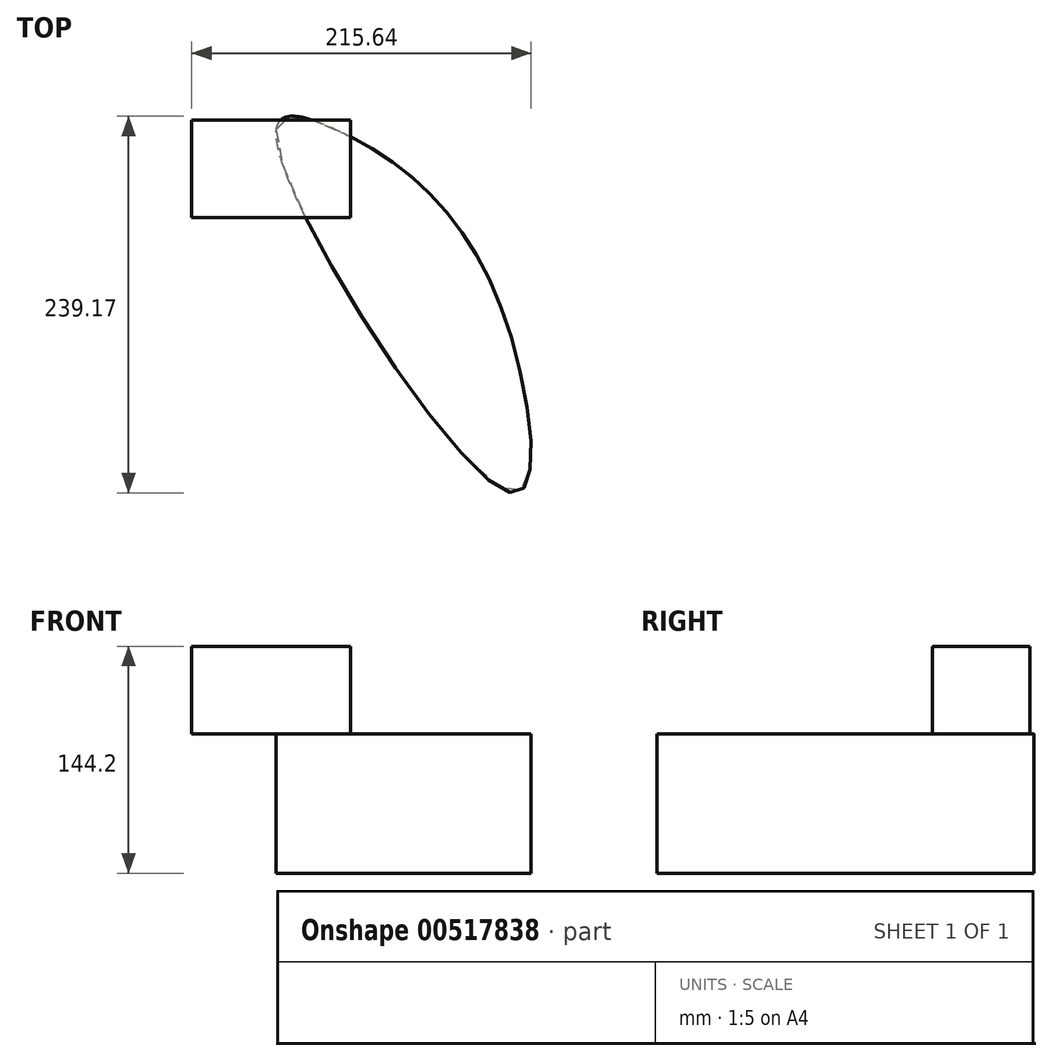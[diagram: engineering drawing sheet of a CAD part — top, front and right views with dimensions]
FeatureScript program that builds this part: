
annotation { "Feature Type Name" : "Feature", "Feature Type Description" : "" }
export const myFeature = defineFeature(function(context is Context, id is Id, definition is map)
    precondition{}
    {
        {
            var Q0;
            Q0=qCreatedBy(makeId("Top.planeOp"),FACE);
            var sketch = newSketch(context, id + "F0", { "sketchPlane" : qUnion([Q0])});
            skFitSpline(sketch, "E0", {"points": [v(-65.64, 81.17) * mm, v(-25.47, 79.82) * mm, v(39.3, 32) * mm, v(88.17, -68.6) * mm, v(82.6, -149.46) * mm, v(-65.64, 81.17) * mm]});
            skSolve(sketch);
        }
        {
            var Q0;
            Q0=makeQuery(id+"F0.imprint","IMPRINT",FACE,{"disambiguationData":[TD([[makeQuery(id+"F0.imprint","IMPRINT",EDGE,{"derivedFrom":sQuery(id+"F0.wireOp",EDGE,"E0")}),-1.0]])]});
            extrude(context, id + "F1", {"entities" : qUnion([Q0]), "depth" : 88.54 * mm, "offsetDistance" : 25.4 * mm});
        }
        {
            var Q0;
            Q0=makeQuery(id+"F1.opExtrude","CAP_FACE",FACE,{"disambiguationData":[OSD([sQuery(id+"F0.wireOp",EDGE,"E0")])],"isStart":false});
            var sketch = newSketch(context, id + "F2", { "sketchPlane" : qUnion([Q0])});
            skLineSegment(sketch, "E1.bottom", {"start": v(-18.72, 25.19) * mm, "end": v(-119.5, 25.19) * mm});
            skLineSegment(sketch, "E1.top", {"start": v(-18.72, 87) * mm, "end": v(-119.5, 87) * mm});
            skLineSegment(sketch, "E1.left", {"start": v(-18.72, 25.19) * mm, "end": v(-18.72, 87) * mm});
            skLineSegment(sketch, "E1.right", {"start": v(-119.5, 25.19) * mm, "end": v(-119.5, 87) * mm});
            skSolve(sketch);
        }
        {
            var Q0;
            Q0 = qSketchRegion(id + "F2", true);
            extrude(context, id + "F3", {"entities" : qUnion([Q0]), "operationType" : NewBodyOperationType.ADD, "depth" : 55.66 * mm, "offsetDistance" : 25.4 * mm});
        }
    });
